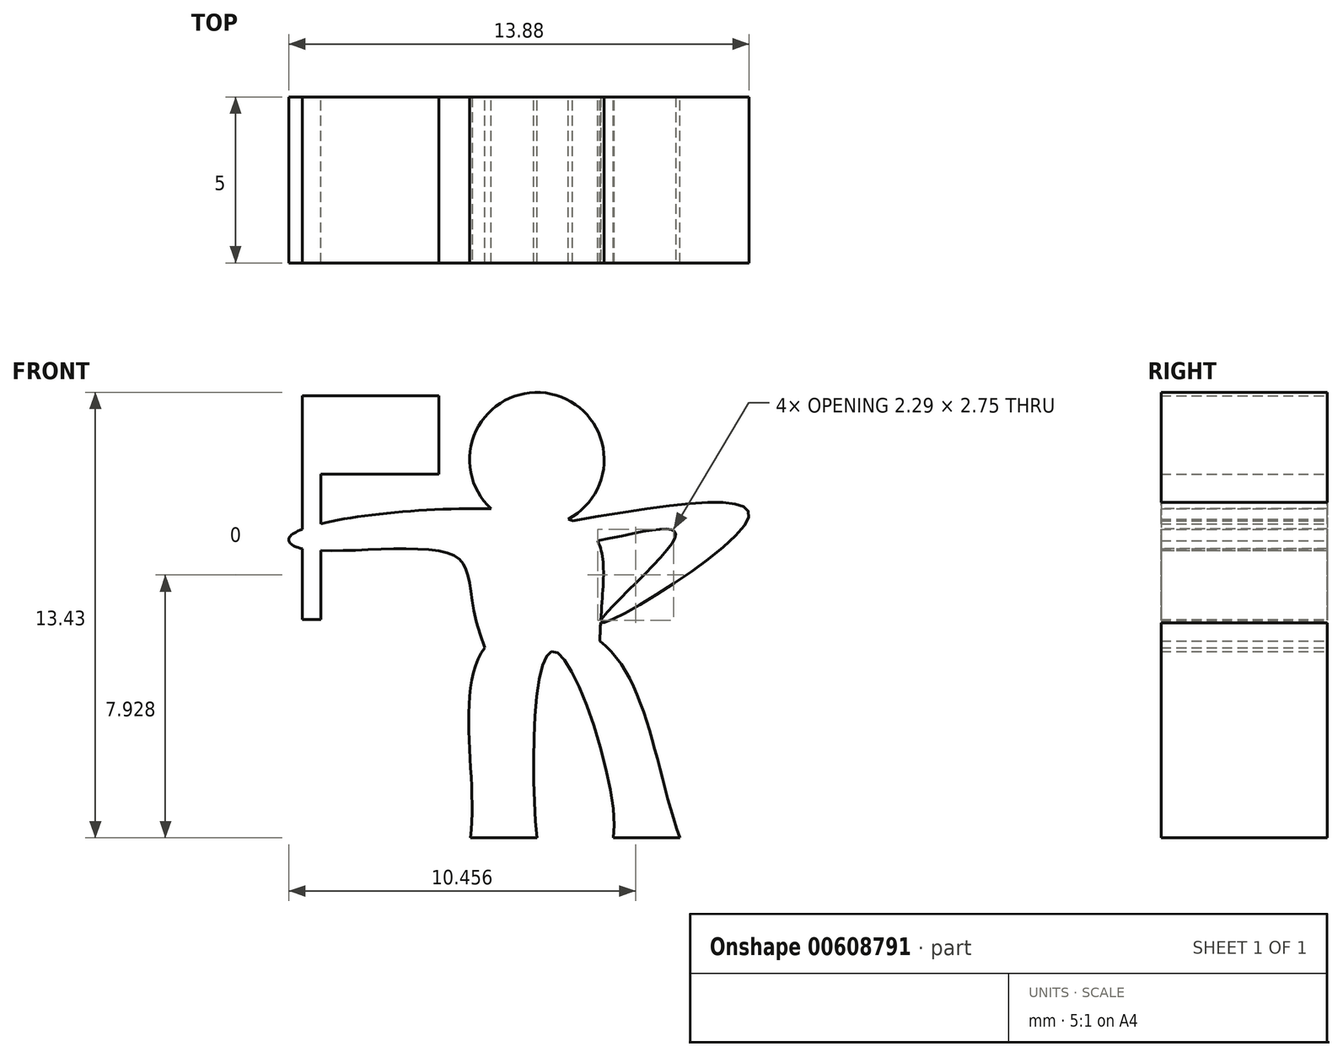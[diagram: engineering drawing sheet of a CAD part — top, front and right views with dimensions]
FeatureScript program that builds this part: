
annotation { "Feature Type Name" : "Feature", "Feature Type Description" : "" }
export const myFeature = defineFeature(function(context is Context, id is Id, definition is map)
    precondition{}
    {
        {
            var Q0;
            Q0=qCreatedBy(makeId("Front.planeOp"),FACE);
            var sketch = newSketch(context, id + "F0", { "sketchPlane" : qUnion([Q0])});
            skLineSegment(sketch, "E0", {"start": v(0, 0) * mm, "end": v(-2, 0) * mm});
            skLineSegment(sketch, "E1", {"start": v(2.3, 0) * mm, "end": v(4.3, 0) * mm});
            skLineSegment(sketch, "E2", {"start": v(4.3, 0) * mm, "end": v(4.3, 0) * mm});
            skLineSegment(sketch, "E3", {"start": v(-2, 0) * mm, "end": v(-2, 0) * mm});
            skFitSpline(sketch, "E4", {"points": [v(0, 0) * mm, v(0.5, 5.62) * mm, v(2.3, 0) * mm], "startDerivative": vector(-1.11, 10.37) * mm, "endDerivative": vector(-1.47, -7.47) * mm});
            skFitSpline(sketch, "E5", {"points": [v(-2, 0) * mm, v(-1.57, 5.74) * mm, v(1.9, 5.93) * mm, v(4.3, 0) * mm], "startDerivative": vector(1.94, 15.36) * mm, "endDerivative": vector(6.14, -17.73) * mm});
            skFitSpline(sketch, "E6", {"points": [v(-1.57, 5.74) * mm, v(-2.56, 8.54) * mm, v(-7.13, 8.73) * mm, v(-7.4, 9.12) * mm, v(1.08, 9.56) * mm, v(1.9, 5.93) * mm], "startDerivative": vector(-10.3, 25.81) * mm, "endDerivative": vector(-0.83, -29.86) * mm});
            skFitSpline(sketch, "E7", {"points": [v(1.08, 9.56) * mm, v(6.34, 9.56) * mm, v(1.92, 6.5) * mm, v(4.17, 9.06) * mm, v(1.83, 8.95) * mm], "startDerivative": vector(31.02, 5.33) * mm, "endDerivative": vector(-21.34, -4.27) * mm});
            skCircle(sketch, "E8", {"center": v(0, 11.4) * mm, "radius": 2.03 * mm});
            skLineSegment(sketch, "E9.bottom", {"start": v(-7.07, 13.33) * mm, "end": v(-6.51, 13.33) * mm});
            skLineSegment(sketch, "E9.top", {"start": v(-7.07, 6.58) * mm, "end": v(-6.51, 6.58) * mm});
            skLineSegment(sketch, "E9.left", {"start": v(-7.07, 13.33) * mm, "end": v(-7.07, 6.58) * mm});
            skLineSegment(sketch, "E9.right", {"start": v(-6.51, 13.33) * mm, "end": v(-6.51, 6.58) * mm});
            skLineSegment(sketch, "E10.bottom", {"start": v(-6.51, 13.33) * mm, "end": v(-2.95, 13.33) * mm});
            skLineSegment(sketch, "E10.top", {"start": v(-6.51, 10.96) * mm, "end": v(-2.95, 10.96) * mm});
            skLineSegment(sketch, "E10.left", {"start": v(-6.51, 13.33) * mm, "end": v(-6.51, 10.96) * mm});
            skLineSegment(sketch, "E10.right", {"start": v(-2.95, 13.33) * mm, "end": v(-2.95, 10.96) * mm});
            skSolve(sketch);
        }
        {
            var Q0;
            Q0 = qSketchRegion(id + "F0", true);
            extrude(context, id + "F1", {"entities" : qUnion([Q0]), "depth" : 5 * mm, "offsetDistance" : 25 * mm});
        }
    });
